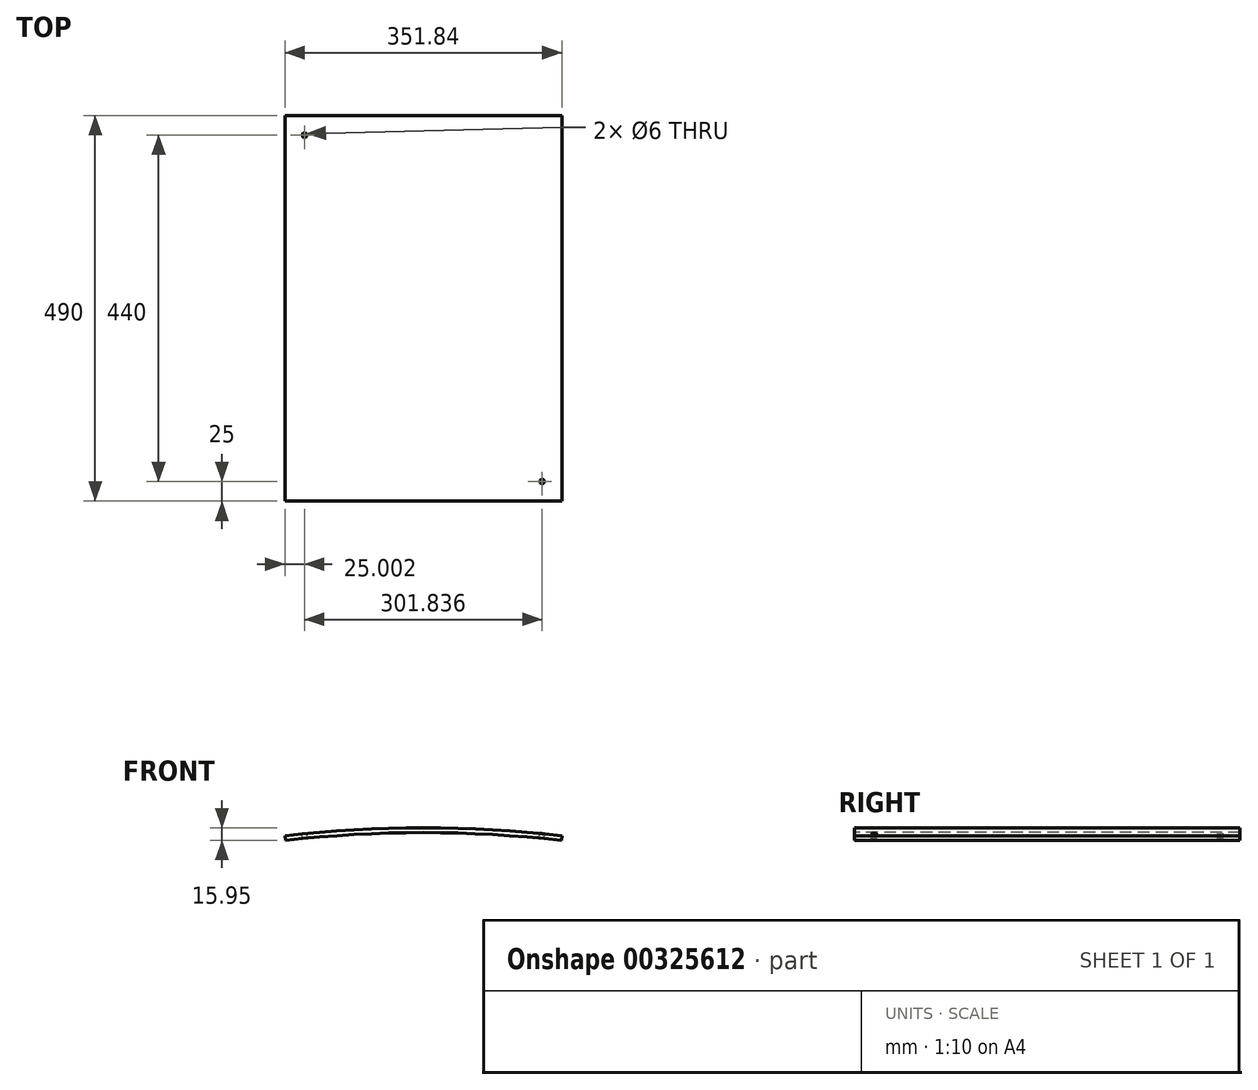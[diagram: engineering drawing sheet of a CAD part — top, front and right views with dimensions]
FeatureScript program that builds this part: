
annotation { "Feature Type Name" : "Feature", "Feature Type Description" : "" }
export const myFeature = defineFeature(function(context is Context, id is Id, definition is map)
    precondition{}
    {
        {
            var Q0;
            Q0=qCreatedBy(makeId("Right.planeOp"),FACE);
            var sketch = newSketch(context, id + "F0", { "sketchPlane" : qUnion([Q0])});
            skLineSegment(sketch, "E0", {"start": v(-75.2, 0) * mm, "end": v(74.8, 0) * mm, "construction": true});
            skLineSegment(sketch, "E1.bottom", {"start": v(245, 1548) * mm, "end": v(-245, 1548) * mm});
            skLineSegment(sketch, "E1.top", {"start": v(245, 1554) * mm, "end": v(-245, 1554) * mm});
            skLineSegment(sketch, "E1.left", {"start": v(245, 1548) * mm, "end": v(245, 1554) * mm});
            skLineSegment(sketch, "E1.right", {"start": v(-245, 1548) * mm, "end": v(-245, 1554) * mm});
            skPoint(sketch, "E1.middle", {"position": v(0, 1551) * mm});
            skSolve(sketch);
        }
        {
            var Q0;
            Q0=makeQuery(id+"F0.imprint","IMPRINT",FACE,{"disambiguationData":[TD([[makeQuery(id+"F0.imprint","IMPRINT",EDGE,{"derivedFrom":sQuery(id+"F0.wireOp",EDGE,"E1.bottom")}),-1.0]])]});
            var Q1;
            Q1=sQuery(id+"F0.wireOp",EDGE,"E0");
            revolve(context, id + "F1", {"entities" : qUnion([Q0]), "axis" : qUnion([Q1]), "revolveType" : RevolveType.SYMMETRIC, "angle" : 13 * degree});
        }
        {
            var Q0;
            Q0=qCreatedBy(makeId("Top.planeOp"),FACE);
            cPlane(context, id + "F2", {"entities" : qUnion([Q0]), "cplaneType" : CPlaneType.OFFSET, "offset" : 1600 * mm, "width" : 150 * mm, "height" : 150 * mm});
        }
        {
            var Q0;
            Q0=qCreatedBy(id+"F2.planeOp",FACE);
            var sketch = newSketch(context, id + "F3", { "sketchPlane" : qUnion([Q0])});
            skCircle(sketch, "E2", {"center": v(-150.92, 220) * mm, "radius": 3 * mm});
            skLineSegment(sketch, "E3", {"start": v(150.49, 0) * mm, "end": v(-149.91, 0) * mm, "construction": true});
            skLineSegment(sketch, "E4", {"start": v(0, 158.55) * mm, "end": v(0, -163.66) * mm, "construction": true});
            skPoint(sketch, "E5", {"position": v(0, 0) * mm});
            skCircle(sketch, "E6.MirrorC", {"center": v(150.92, 220) * mm, "radius": 3 * mm});
            skLineSegment(sketch, "E7.MirrorCS", {"start": v(-150.49, 0) * mm, "end": v(149.91, 0) * mm, "construction": true});
            skCircle(sketch, "E8.MirrorC", {"center": v(150.92, -220) * mm, "radius": 3 * mm});
            skSolve(sketch);
        }
        {
            var Q0;
            Q0=sQuery(id+"F3.wireOp",VERTEX,"E2.center");
            var Q1;
            Q1=sQuery(id+"F3.wireOp",VERTEX,"E8.MirrorC.center");
            var Q2;
            Q2=makeQuery(id+"F1.opRevolve","SWEPT_BODY",BODY,{"disambiguationData":[OSD([sQuery(id+"F0.wireOp",EDGE,"E1.bottom"),sQuery(id+"F0.wireOp",EDGE,"E1.top"),sQuery(id+"F0.wireOp",EDGE,"E1.left"),sQuery(id+"F0.wireOp",EDGE,"E1.right")])]});
            hole(context, id + "F4", {"style" : HoleStyle.SIMPLE, "endStyle" : HoleEndStyle.BLIND, "holeDiameter" : 6 * mm, "holeDepth" : 100 * mm, "tappedDepth" : 12 * mm, "tapClearance" : 3, "startFromSketch" : true, "locations" : qUnion([Q0, Q1]), "scope" : qUnion([Q2])});
        }
    });
